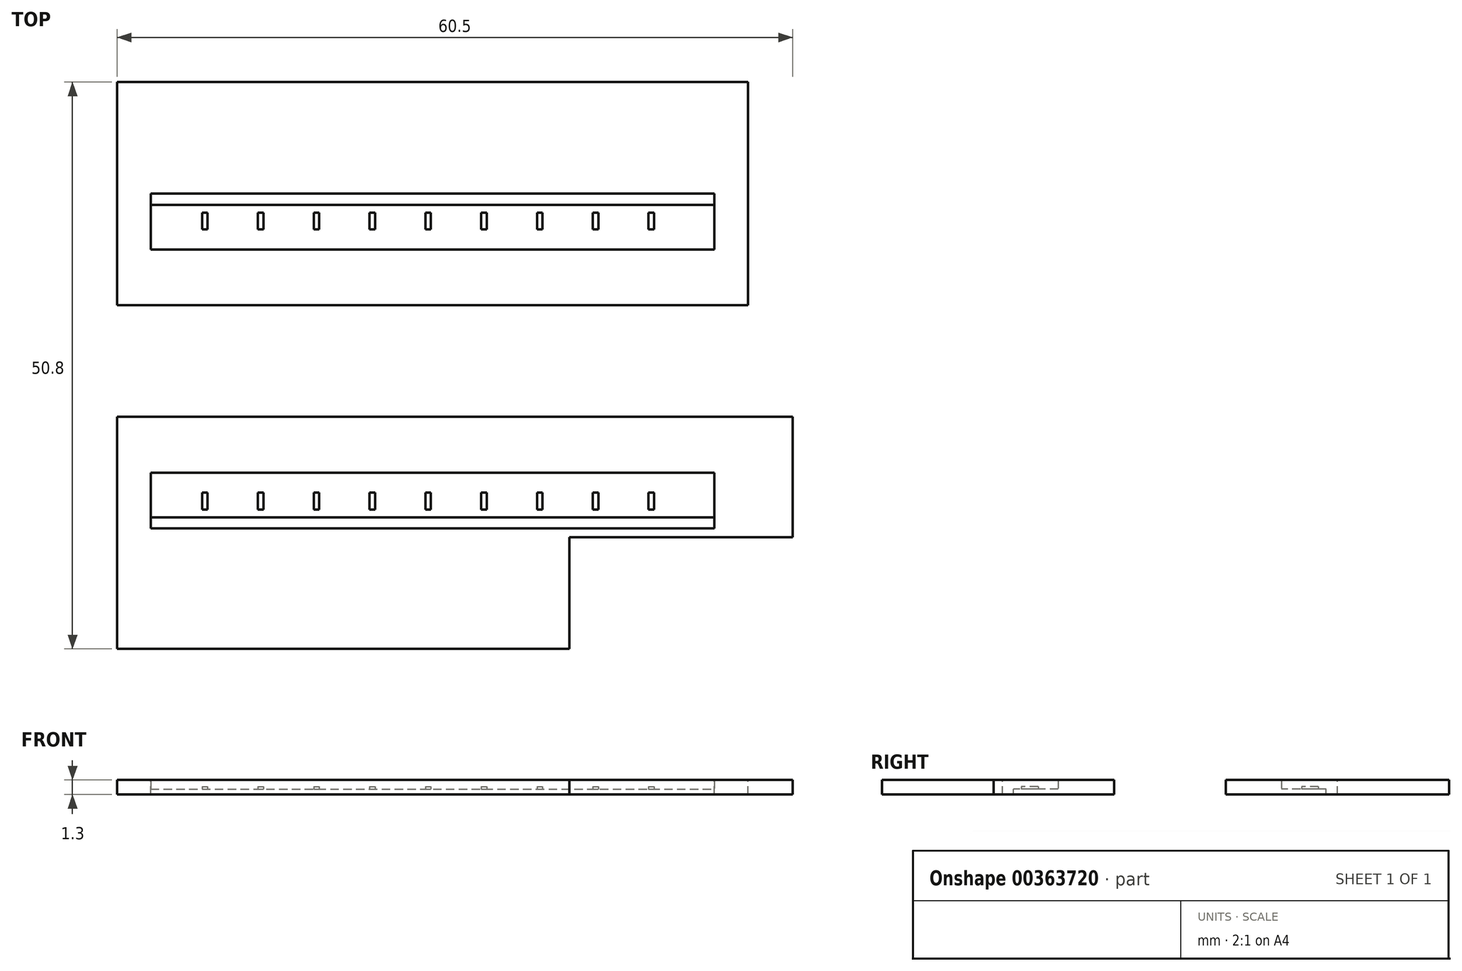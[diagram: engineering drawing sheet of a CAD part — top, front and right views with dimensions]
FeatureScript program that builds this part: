
annotation { "Feature Type Name" : "Feature", "Feature Type Description" : "" }
export const myFeature = defineFeature(function(context is Context, id is Id, definition is map)
    precondition{}
    {
        {
            var Q0;
            Q0=qCreatedBy(makeId("Top.planeOp"),FACE);
            var sketch = newSketch(context, id + "F0", { "sketchPlane" : qUnion([Q0])});
            skLineSegment(sketch, "E0.bottom", {"start": v(-66.5, 25) * mm, "end": v(-10, 25) * mm});
            skLineSegment(sketch, "E0.top", {"start": v(-66.5, 5) * mm, "end": v(-10, 5) * mm});
            skLineSegment(sketch, "E0.left", {"start": v(-66.5, 25) * mm, "end": v(-66.5, 5) * mm});
            skLineSegment(sketch, "E0.right", {"start": v(-10, 25) * mm, "end": v(-10, 5) * mm});
            skLineSegment(sketch, "E1.bottom", {"start": v(-63.5, 14) * mm, "end": v(-13, 14) * mm});
            skLineSegment(sketch, "E1.top", {"start": v(-63.5, 10) * mm, "end": v(-13, 10) * mm});
            skLineSegment(sketch, "E1.left", {"start": v(-63.5, 14) * mm, "end": v(-63.5, 10) * mm});
            skLineSegment(sketch, "E1.right", {"start": v(-13, 14) * mm, "end": v(-13, 10) * mm});
            skLineSegment(sketch, "E2", {"start": v(-38.25, 25) * mm, "end": v(-38.25, 5) * mm, "construction": true});
            skPoint(sketch, "E3", {"position": v(-38.25, 14) * mm});
            skLineSegment(sketch, "E4.top", {"start": v(-63.5, 15) * mm, "end": v(-13, 15) * mm});
            skLineSegment(sketch, "E4.left", {"start": v(-63.5, 14) * mm, "end": v(-63.5, 15) * mm});
            skLineSegment(sketch, "E4.right", {"start": v(-13, 14) * mm, "end": v(-13, 15) * mm});
            skLineSegment(sketch, "E5.bottom", {"start": v(-63.5, -14) * mm, "end": v(-13, -14) * mm});
            skLineSegment(sketch, "E5.top", {"start": v(-63.5, -10) * mm, "end": v(-13, -10) * mm});
            skLineSegment(sketch, "E5.left", {"start": v(-63.5, -14) * mm, "end": v(-63.5, -10) * mm});
            skLineSegment(sketch, "E5.right", {"start": v(-13, -14) * mm, "end": v(-13, -10) * mm});
            skLineSegment(sketch, "E6.top", {"start": v(-63.5, -15) * mm, "end": v(-13, -15) * mm});
            skLineSegment(sketch, "E6.left", {"start": v(-63.5, -14) * mm, "end": v(-63.5, -15) * mm});
            skLineSegment(sketch, "E6.right", {"start": v(-13, -14) * mm, "end": v(-13, -15) * mm});
            skLineSegment(sketch, "E7.bottom", {"start": v(-66.5, -5) * mm, "end": v(-6, -5) * mm});
            skLineSegment(sketch, "E7.top", {"start": v(-66.5, -25.8) * mm, "end": v(-6, -25.8) * mm});
            skLineSegment(sketch, "E7.left", {"start": v(-66.5, -5) * mm, "end": v(-66.5, -25.8) * mm});
            skLineSegment(sketch, "E7.right", {"start": v(-6, -5) * mm, "end": v(-6, -25.8) * mm});
            skLineSegment(sketch, "E8.bottom", {"start": v(-26, -15.8) * mm, "end": v(-13, -15.8) * mm});
            skLineSegment(sketch, "E8.top", {"start": v(-26, -20.8) * mm, "end": v(-13, -20.8) * mm});
            skLineSegment(sketch, "E8.left", {"start": v(-26, -15.8) * mm, "end": v(-26, -20.8) * mm});
            skLineSegment(sketch, "E8.right", {"start": v(-13, -15.8) * mm, "end": v(-13, -20.8) * mm});
            skLineSegment(sketch, "E9", {"start": v(-26, -20.8) * mm, "end": v(-26, -25.8) * mm});
            skLineSegment(sketch, "E10", {"start": v(-24, -20.8) * mm, "end": v(-24, -25.8) * mm});
            skLineSegment(sketch, "E11", {"start": v(-13, -15.8) * mm, "end": v(-6, -15.8) * mm});
            skLineSegment(sketch, "E12", {"start": v(-13, -17.8) * mm, "end": v(-6, -17.8) * mm});
            skSolve(sketch);
        }
        {
            var Q0;
            Q0=makeQuery(id+"F0.imprint","IMPRINT",FACE,{"disambiguationData":[TD([[makeQuery(id+"F0.imprint","IMPRINT",EDGE,{"derivedFrom":sQuery(id+"F0.wireOp",EDGE,"E0.bottom")}),-1.0]])]});
            var Q1;
            Q1=makeQuery(id+"F0.imprint","IMPRINT",FACE,{"disambiguationData":[TD([[makeQuery(id+"F0.imprint","IMPRINT",EDGE,{"derivedFrom":sQuery(id+"F0.wireOp",EDGE,"E1.top")}),1.0]])]});
            var Q2;
            Q2=makeQuery(id+"F0.imprint","IMPRINT",FACE,{"disambiguationData":[TD([[makeQuery(id+"F0.imprint","IMPRINT",EDGE,{"derivedFrom":sQuery(id+"F0.wireOp",EDGE,"E5.top")}),1.0]])]});
            var Q3;
            Q3=makeQuery(id+"F0.imprint","IMPRINT",FACE,{"disambiguationData":[TD([[makeQuery(id+"F0.imprint","IMPRINT",EDGE,{"derivedFrom":sQuery(id+"F0.wireOp",EDGE,"E5.top")}),-1.0]])]});
            extrude(context, id + "F1", {"entities" : qUnion([Q0, Q1, Q2, Q3]), "oppositeDirection" : true, "depth" : 0.5 * mm});
        }
        {
            var Q0;
            Q0=makeQuery(id+"F0.imprint","IMPRINT",FACE,{"disambiguationData":[TD([[makeQuery(id+"F0.imprint","IMPRINT",EDGE,{"derivedFrom":sQuery(id+"F0.wireOp",EDGE,"E0.bottom")}),-1.0]])]});
            extrude(context, id + "F2", {"entities" : qUnion([Q0]), "operationType" : NewBodyOperationType.ADD, "depth" : 0.8 * mm});
        }
        {
            var Q0;
            Q0=makeQuery(id+"F1.opExtrude","CAP_FACE",FACE,{"disambiguationData":[OSD([sQuery(id+"F0.wireOp",EDGE,"E0.bottom"),sQuery(id+"F0.wireOp",EDGE,"E0.top"),sQuery(id+"F0.wireOp",EDGE,"E0.left"),sQuery(id+"F0.wireOp",EDGE,"E0.right"),sQuery(id+"F0.wireOp",EDGE,"E1.bottom"),sQuery(id+"F0.wireOp",EDGE,"E4.top"),sQuery(id+"F0.wireOp",EDGE,"E4.left"),sQuery(id+"F0.wireOp",EDGE,"E4.right")])],"isStart":true});
            var sketch = newSketch(context, id + "F3", { "sketchPlane" : qUnion([Q0])});
            skLineSegment(sketch, "E13.bottom", {"start": v(-58.9, 13.3) * mm, "end": v(-58.4, 13.3) * mm});
            skLineSegment(sketch, "E13.top", {"start": v(-58.9, 11.8) * mm, "end": v(-58.4, 11.8) * mm});
            skLineSegment(sketch, "E13.left", {"start": v(-58.9, 13.3) * mm, "end": v(-58.9, 11.8) * mm});
            skLineSegment(sketch, "E13.right", {"start": v(-58.4, 13.3) * mm, "end": v(-58.4, 11.8) * mm});
            skLineSegment(sketch, "E14.1.0.0", {"start": v(-53.4, 13.3) * mm, "end": v(-53.4, 11.8) * mm});
            skLineSegment(sketch, "E14.1.0.1", {"start": v(-53.9, 13.3) * mm, "end": v(-53.4, 13.3) * mm});
            skLineSegment(sketch, "E14.1.0.2", {"start": v(-53.9, 13.3) * mm, "end": v(-53.9, 11.8) * mm});
            skLineSegment(sketch, "E14.1.0.3", {"start": v(-53.9, 11.8) * mm, "end": v(-53.4, 11.8) * mm});
            skLineSegment(sketch, "E14.2.0.0", {"start": v(-48.4, 13.3) * mm, "end": v(-48.4, 11.8) * mm});
            skLineSegment(sketch, "E14.2.0.1", {"start": v(-48.9, 13.3) * mm, "end": v(-48.4, 13.3) * mm});
            skLineSegment(sketch, "E14.2.0.2", {"start": v(-48.9, 13.3) * mm, "end": v(-48.9, 11.8) * mm});
            skLineSegment(sketch, "E14.2.0.3", {"start": v(-48.9, 11.8) * mm, "end": v(-48.4, 11.8) * mm});
            skLineSegment(sketch, "E14.3.0.0", {"start": v(-43.4, 13.3) * mm, "end": v(-43.4, 11.8) * mm});
            skLineSegment(sketch, "E14.3.0.1", {"start": v(-43.9, 13.3) * mm, "end": v(-43.4, 13.3) * mm});
            skLineSegment(sketch, "E14.3.0.2", {"start": v(-43.9, 13.3) * mm, "end": v(-43.9, 11.8) * mm});
            skLineSegment(sketch, "E14.3.0.3", {"start": v(-43.9, 11.8) * mm, "end": v(-43.4, 11.8) * mm});
            skLineSegment(sketch, "E14.4.0.0", {"start": v(-38.4, 13.3) * mm, "end": v(-38.4, 11.8) * mm});
            skLineSegment(sketch, "E14.4.0.1", {"start": v(-38.9, 13.3) * mm, "end": v(-38.4, 13.3) * mm});
            skLineSegment(sketch, "E14.4.0.2", {"start": v(-38.9, 13.3) * mm, "end": v(-38.9, 11.8) * mm});
            skLineSegment(sketch, "E14.4.0.3", {"start": v(-38.9, 11.8) * mm, "end": v(-38.4, 11.8) * mm});
            skLineSegment(sketch, "E14.5.0.0", {"start": v(-33.4, 13.3) * mm, "end": v(-33.4, 11.8) * mm});
            skLineSegment(sketch, "E14.5.0.1", {"start": v(-33.9, 13.3) * mm, "end": v(-33.4, 13.3) * mm});
            skLineSegment(sketch, "E14.5.0.2", {"start": v(-33.9, 13.3) * mm, "end": v(-33.9, 11.8) * mm});
            skLineSegment(sketch, "E14.5.0.3", {"start": v(-33.9, 11.8) * mm, "end": v(-33.4, 11.8) * mm});
            skLineSegment(sketch, "E14.6.0.0", {"start": v(-28.4, 13.3) * mm, "end": v(-28.4, 11.8) * mm});
            skLineSegment(sketch, "E14.6.0.1", {"start": v(-28.9, 13.3) * mm, "end": v(-28.4, 13.3) * mm});
            skLineSegment(sketch, "E14.6.0.2", {"start": v(-28.9, 13.3) * mm, "end": v(-28.9, 11.8) * mm});
            skLineSegment(sketch, "E14.6.0.3", {"start": v(-28.9, 11.8) * mm, "end": v(-28.4, 11.8) * mm});
            skLineSegment(sketch, "E14.7.0.0", {"start": v(-23.4, 13.3) * mm, "end": v(-23.4, 11.8) * mm});
            skLineSegment(sketch, "E14.7.0.1", {"start": v(-23.9, 13.3) * mm, "end": v(-23.4, 13.3) * mm});
            skLineSegment(sketch, "E14.7.0.2", {"start": v(-23.9, 13.3) * mm, "end": v(-23.9, 11.8) * mm});
            skLineSegment(sketch, "E14.7.0.3", {"start": v(-23.9, 11.8) * mm, "end": v(-23.4, 11.8) * mm});
            skLineSegment(sketch, "E14.8.0.0", {"start": v(-18.4, 13.3) * mm, "end": v(-18.4, 11.8) * mm});
            skLineSegment(sketch, "E14.8.0.1", {"start": v(-18.9, 13.3) * mm, "end": v(-18.4, 13.3) * mm});
            skLineSegment(sketch, "E14.8.0.2", {"start": v(-18.9, 13.3) * mm, "end": v(-18.9, 11.8) * mm});
            skLineSegment(sketch, "E14.8.0.3", {"start": v(-18.9, 11.8) * mm, "end": v(-18.4, 11.8) * mm});
            skLineSegment(sketch, "E14.direction1", {"start": v(-58.9, 11.8) * mm, "end": v(-53.9, 11.8) * mm, "construction": true});
            skSolve(sketch);
        }
        {
            var Q0;
            Q0 = qSketchRegion(id + "F3", true);
            extrude(context, id + "F4", {"entities" : qUnion([Q0]), "operationType" : NewBodyOperationType.ADD, "depth" : 0.2 * mm});
        }
        {
            var Q0;
            Q0=makeQuery(id+"F0.imprint","IMPRINT",FACE,{"disambiguationData":[TD([[makeQuery(id+"F0.imprint","IMPRINT",EDGE,{"derivedFrom":sQuery(id+"F0.wireOp",EDGE,"E5.top")}),1.0]])]});
            extrude(context, id + "F5", {"entities" : qUnion([Q0]), "operationType" : NewBodyOperationType.ADD, "depth" : 0.8 * mm});
        }
        {
            var Q0;
            Q0=makeQuery(id+"F1.opExtrude","CAP_FACE",FACE,{"disambiguationData":[OSD([sQuery(id+"F0.wireOp",EDGE,"E5.bottom"),sQuery(id+"F0.wireOp",EDGE,"E6.top"),sQuery(id+"F0.wireOp",EDGE,"E6.left"),sQuery(id+"F0.wireOp",EDGE,"E6.right"),sQuery(id+"F0.wireOp",EDGE,"E7.bottom"),sQuery(id+"F0.wireOp",EDGE,"E7.top"),sQuery(id+"F0.wireOp",EDGE,"E7.left"),sQuery(id+"F0.wireOp",EDGE,"E7.right"),sQuery(id+"F0.wireOp",EDGE,"E8.bottom"),sQuery(id+"F0.wireOp",EDGE,"E8.left"),sQuery(id+"F0.wireOp",EDGE,"E9"),sQuery(id+"F0.wireOp",EDGE,"E11")])],"isStart":true});
            var sketch = newSketch(context, id + "F6", { "sketchPlane" : qUnion([Q0])});
            skLineSegment(sketch, "E15.bottom", {"start": v(-58.9, -11.8) * mm, "end": v(-58.4, -11.8) * mm});
            skLineSegment(sketch, "E15.top", {"start": v(-58.9, -13.3) * mm, "end": v(-58.4, -13.3) * mm});
            skLineSegment(sketch, "E15.left", {"start": v(-58.9, -11.8) * mm, "end": v(-58.9, -13.3) * mm});
            skLineSegment(sketch, "E15.right", {"start": v(-58.4, -11.8) * mm, "end": v(-58.4, -13.3) * mm});
            skLineSegment(sketch, "E16", {"start": v(-58.9, -13.3) * mm, "end": v(-63.5, -13.3) * mm, "construction": true});
            skLineSegment(sketch, "E17", {"start": v(-58.4, -11.8) * mm, "end": v(-58.4, -10) * mm, "construction": true});
            skLineSegment(sketch, "E18.1.0.0", {"start": v(-53.9, -11.8) * mm, "end": v(-53.9, -13.3) * mm});
            skLineSegment(sketch, "E18.1.0.1", {"start": v(-53.9, -11.8) * mm, "end": v(-53.4, -11.8) * mm});
            skLineSegment(sketch, "E18.1.0.2", {"start": v(-53.4, -11.8) * mm, "end": v(-53.4, -13.3) * mm});
            skLineSegment(sketch, "E18.1.0.3", {"start": v(-53.9, -13.3) * mm, "end": v(-53.4, -13.3) * mm});
            skLineSegment(sketch, "E18.2.0.0", {"start": v(-48.9, -11.8) * mm, "end": v(-48.9, -13.3) * mm});
            skLineSegment(sketch, "E18.2.0.1", {"start": v(-48.9, -11.8) * mm, "end": v(-48.4, -11.8) * mm});
            skLineSegment(sketch, "E18.2.0.2", {"start": v(-48.4, -11.8) * mm, "end": v(-48.4, -13.3) * mm});
            skLineSegment(sketch, "E18.2.0.3", {"start": v(-48.9, -13.3) * mm, "end": v(-48.4, -13.3) * mm});
            skLineSegment(sketch, "E18.3.0.0", {"start": v(-43.9, -11.8) * mm, "end": v(-43.9, -13.3) * mm});
            skLineSegment(sketch, "E18.3.0.1", {"start": v(-43.9, -11.8) * mm, "end": v(-43.4, -11.8) * mm});
            skLineSegment(sketch, "E18.3.0.2", {"start": v(-43.4, -11.8) * mm, "end": v(-43.4, -13.3) * mm});
            skLineSegment(sketch, "E18.3.0.3", {"start": v(-43.9, -13.3) * mm, "end": v(-43.4, -13.3) * mm});
            skLineSegment(sketch, "E18.4.0.0", {"start": v(-38.9, -11.8) * mm, "end": v(-38.9, -13.3) * mm});
            skLineSegment(sketch, "E18.4.0.1", {"start": v(-38.9, -11.8) * mm, "end": v(-38.4, -11.8) * mm});
            skLineSegment(sketch, "E18.4.0.2", {"start": v(-38.4, -11.8) * mm, "end": v(-38.4, -13.3) * mm});
            skLineSegment(sketch, "E18.4.0.3", {"start": v(-38.9, -13.3) * mm, "end": v(-38.4, -13.3) * mm});
            skLineSegment(sketch, "E18.5.0.0", {"start": v(-33.9, -11.8) * mm, "end": v(-33.9, -13.3) * mm});
            skLineSegment(sketch, "E18.5.0.1", {"start": v(-33.9, -11.8) * mm, "end": v(-33.4, -11.8) * mm});
            skLineSegment(sketch, "E18.5.0.2", {"start": v(-33.4, -11.8) * mm, "end": v(-33.4, -13.3) * mm});
            skLineSegment(sketch, "E18.5.0.3", {"start": v(-33.9, -13.3) * mm, "end": v(-33.4, -13.3) * mm});
            skLineSegment(sketch, "E18.6.0.0", {"start": v(-28.9, -11.8) * mm, "end": v(-28.9, -13.3) * mm});
            skLineSegment(sketch, "E18.6.0.1", {"start": v(-28.9, -11.8) * mm, "end": v(-28.4, -11.8) * mm});
            skLineSegment(sketch, "E18.6.0.2", {"start": v(-28.4, -11.8) * mm, "end": v(-28.4, -13.3) * mm});
            skLineSegment(sketch, "E18.6.0.3", {"start": v(-28.9, -13.3) * mm, "end": v(-28.4, -13.3) * mm});
            skLineSegment(sketch, "E18.7.0.0", {"start": v(-23.9, -11.8) * mm, "end": v(-23.9, -13.3) * mm});
            skLineSegment(sketch, "E18.7.0.1", {"start": v(-23.9, -11.8) * mm, "end": v(-23.4, -11.8) * mm});
            skLineSegment(sketch, "E18.7.0.2", {"start": v(-23.4, -11.8) * mm, "end": v(-23.4, -13.3) * mm});
            skLineSegment(sketch, "E18.7.0.3", {"start": v(-23.9, -13.3) * mm, "end": v(-23.4, -13.3) * mm});
            skLineSegment(sketch, "E18.8.0.0", {"start": v(-18.9, -11.8) * mm, "end": v(-18.9, -13.3) * mm});
            skLineSegment(sketch, "E18.8.0.1", {"start": v(-18.9, -11.8) * mm, "end": v(-18.4, -11.8) * mm});
            skLineSegment(sketch, "E18.8.0.2", {"start": v(-18.4, -11.8) * mm, "end": v(-18.4, -13.3) * mm});
            skLineSegment(sketch, "E18.8.0.3", {"start": v(-18.9, -13.3) * mm, "end": v(-18.4, -13.3) * mm});
            skLineSegment(sketch, "E18.direction1", {"start": v(-58.9, -13.3) * mm, "end": v(-53.9, -13.3) * mm, "construction": true});
            skSolve(sketch);
        }
        {
            var Q0;
            Q0 = qSketchRegion(id + "F6", true);
            extrude(context, id + "F7", {"entities" : qUnion([Q0]), "operationType" : NewBodyOperationType.ADD, "depth" : 0.2 * mm});
        }
    });
